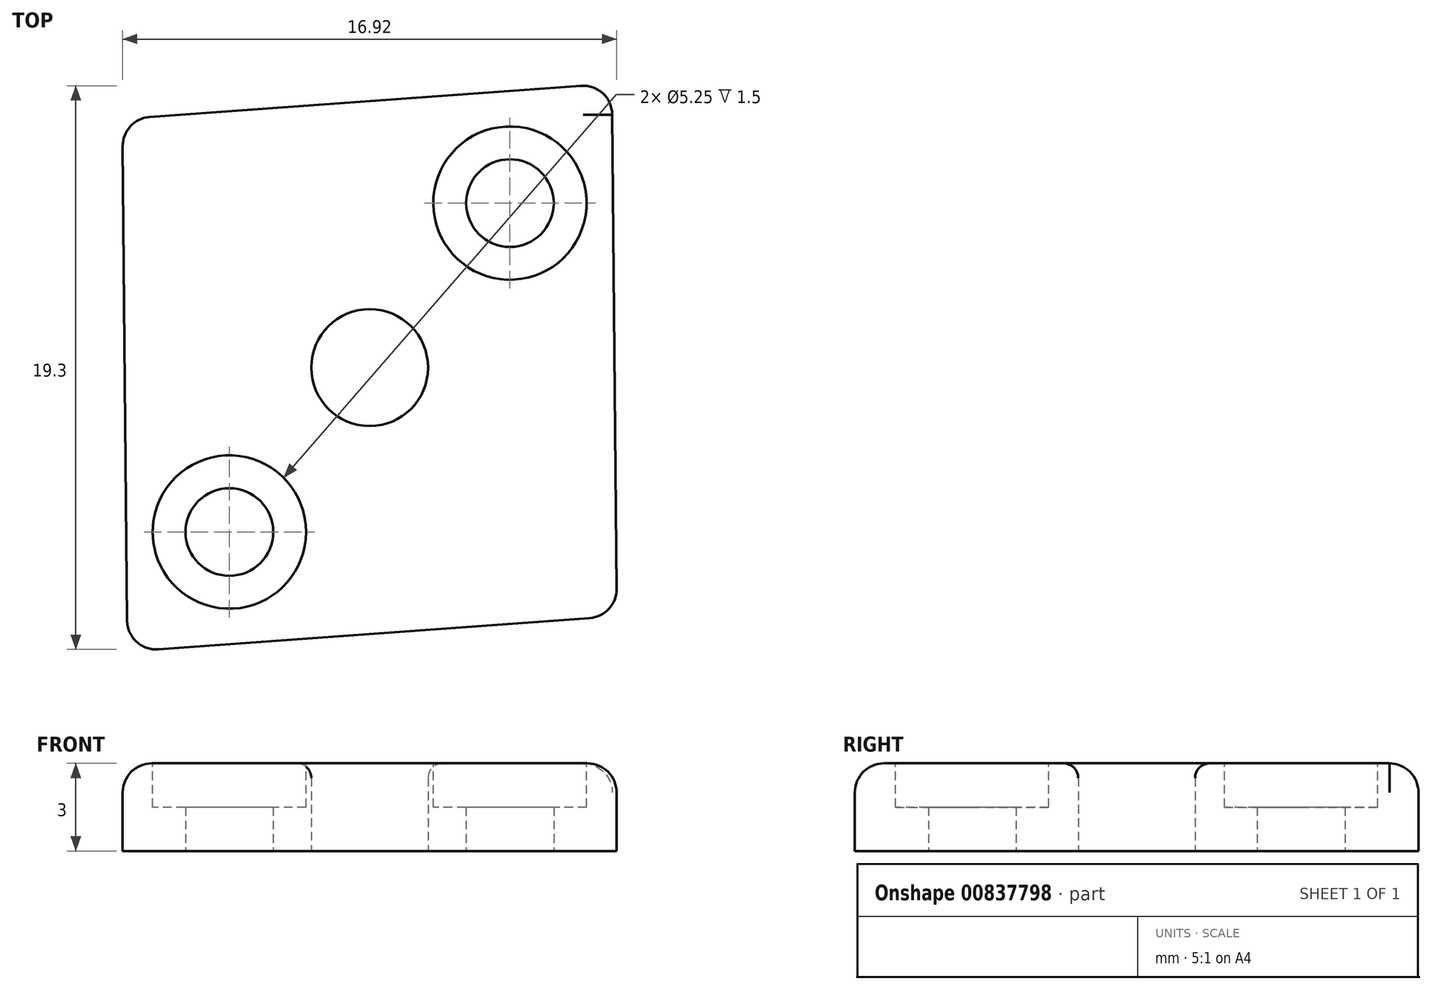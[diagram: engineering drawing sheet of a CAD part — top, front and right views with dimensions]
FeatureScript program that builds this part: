
annotation { "Feature Type Name" : "Feature", "Feature Type Description" : "" }
export const myFeature = defineFeature(function(context is Context, id is Id, definition is map)
    precondition{}
    {
        {
            var Q0;
            Q0=qCreatedBy(makeId("Top.planeOp"),FACE);
            var sketch = newSketch(context, id + "F0", { "sketchPlane" : qUnion([Q0])});
            skLineSegment(sketch, "E0", {"start": v(6.35, -6.39) * mm, "end": v(-6.35, 6.39) * mm, "construction": true});
            skLineSegment(sketch, "E1", {"start": v(6.35, 7.44) * mm, "end": v(-6.35, -7.44) * mm, "construction": true});
            skLineSegment(sketch, "E2", {"start": v(-6.35, -7.44) * mm, "end": v(-8.3, -9.73) * mm, "construction": true});
            skLineSegment(sketch, "E3", {"start": v(6.35, -6.39) * mm, "end": v(8.46, -8.51) * mm, "construction": true});
            skLineSegment(sketch, "E4", {"start": v(6.35, 7.44) * mm, "end": v(8.3, 9.73) * mm, "construction": true});
            skLineSegment(sketch, "E5", {"start": v(-6.35, 6.39) * mm, "end": v(-8.46, 8.51) * mm, "construction": true});
            skLineSegment(sketch, "E6", {"start": v(8.3, 9.73) * mm, "end": v(8.46, -8.51) * mm});
            skLineSegment(sketch, "E7", {"start": v(8.46, -8.51) * mm, "end": v(-8.3, -9.73) * mm});
            skLineSegment(sketch, "E8", {"start": v(-8.3, -9.73) * mm, "end": v(-8.46, 8.51) * mm});
            skLineSegment(sketch, "E9", {"start": v(-8.46, 8.51) * mm, "end": v(8.3, 9.73) * mm});
            skCircle(sketch, "E10", {"center": v(0, 0) * mm, "radius": 2 * mm});
            skLineSegment(sketch, "E11", {"start": v(0, 0) * mm, "end": v(-0.85, -1.8) * mm, "construction": true});
            skLineSegment(sketch, "E12", {"start": v(0, 0) * mm, "end": v(1.14, -1.64) * mm, "construction": true});
            skLineSegment(sketch, "E13", {"start": v(0, 0) * mm, "end": v(-1.14, 1.64) * mm, "construction": true});
            skLineSegment(sketch, "E14", {"start": v(0, 0) * mm, "end": v(0.85, 1.8) * mm, "construction": true});
            skLineSegment(sketch, "E15", {"start": v(-0.85, -1.8) * mm, "end": v(-1.72, -3.66) * mm, "construction": true});
            skLineSegment(sketch, "E16", {"start": v(0.85, 1.8) * mm, "end": v(1.72, 3.66) * mm, "construction": true});
            skLineSegment(sketch, "E17", {"start": v(-1.14, 1.64) * mm, "end": v(-2.3, 3.32) * mm, "construction": true});
            skLineSegment(sketch, "E18", {"start": v(1.14, -1.64) * mm, "end": v(2.3, -3.32) * mm, "construction": true});
            skLineSegment(sketch, "E19", {"start": v(6.35, 0.53) * mm, "end": v(-6.35, -0.53) * mm, "construction": true});
            skLineSegment(sketch, "E20", {"start": v(2.3, -3.32) * mm, "end": v(-1.72, -3.66) * mm});
            skLineSegment(sketch, "E21", {"start": v(1.72, 3.66) * mm, "end": v(-2.3, 3.32) * mm});
            skLineSegment(sketch, "E22", {"start": v(2, 0.17) * mm, "end": v(4.03, 0.34) * mm, "construction": true});
            skLineSegment(sketch, "E23", {"start": v(-2, -0.17) * mm, "end": v(-4.03, -0.34) * mm, "construction": true});
            skLineSegment(sketch, "E24", {"start": v(4.03, 0.34) * mm, "end": v(2.3, -3.32) * mm});
            skLineSegment(sketch, "E25", {"start": v(-1.72, -3.66) * mm, "end": v(-4.03, -0.34) * mm});
            skLineSegment(sketch, "E26", {"start": v(-4.03, -0.34) * mm, "end": v(-2.3, 3.32) * mm});
            skLineSegment(sketch, "E27", {"start": v(1.72, 3.66) * mm, "end": v(4.03, 0.34) * mm});
            skLineSegment(sketch, "E28", {"start": v(8.3, 9.73) * mm, "end": v(2.35, 2.75) * mm, "construction": true});
            skLineSegment(sketch, "E29", {"start": v(-2.35, -2.75) * mm, "end": v(-8.3, -9.73) * mm, "construction": true});
            skLineSegment(sketch, "E30", {"start": v(5.32, 6.24) * mm, "end": v(4.8, 5.63) * mm, "construction": true});
            skLineSegment(sketch, "E31", {"start": v(-5.32, -6.24) * mm, "end": v(-4.8, -5.63) * mm, "construction": true});
            skCircle(sketch, "E32", {"center": v(4.8, 5.63) * mm, "radius": 1.5 * mm});
            skCircle(sketch, "E33", {"center": v(-4.8, -5.63) * mm, "radius": 1.5 * mm});
            skSolve(sketch);
        }
        {
            var Q0;
            Q0 = qSketchRegion(id + "F0", true);
            var Q1;
            Q1=makeQuery(id+"F0.imprint","IMPRINT",FACE,{"disambiguationData":[TD([[makeQuery(id+"F0.imprint","IMPRINT",EDGE,{"derivedFrom":sQuery(id+"F0.wireOp",EDGE,"E10")}),-1.0]])]});
            extrude(context, id + "F1", {"entities" : qUnion([Q0, Q1]), "depth" : 3 * mm, "offsetDistance" : 25 * mm});
        }
        {
            var Q0;
            Q0=makeQuery(id+"F1.opExtrude","CAP_FACE",FACE,{"disambiguationData":[OSD([sQuery(id+"F0.wireOp",EDGE,"E6"),sQuery(id+"F0.wireOp",EDGE,"E7"),sQuery(id+"F0.wireOp",EDGE,"E8"),sQuery(id+"F0.wireOp",EDGE,"E9"),sQuery(id+"F0.wireOp",EDGE,"E10"),sQuery(id+"F0.wireOp",EDGE,"E32"),sQuery(id+"F0.wireOp",EDGE,"E33")])],"isStart":false});
            var sketch = newSketch(context, id + "F2", { "sketchPlane" : qUnion([Q0])});
            skCircle(sketch, "E34", {"center": v(-4.8, -5.63) * mm, "radius": 2.62 * mm});
            skCircle(sketch, "E35", {"center": v(4.8, 5.63) * mm, "radius": 2.62 * mm});
            skSolve(sketch);
        }
        {
            var Q0;
            Q0=makeQuery(id+"F2.imprint","IMPRINT",FACE,{"disambiguationData":[TD([[makeQuery(id+"F2.imprint","IMPRINT",EDGE,{"derivedFrom":sQuery(id+"F2.wireOp",EDGE,"E34")}),1.0]])]});
            var Q1;
            Q1=makeQuery(id+"F2.imprint","IMPRINT",FACE,{"disambiguationData":[TD([[makeQuery(id+"F2.imprint","IMPRINT",EDGE,{"derivedFrom":sQuery(id+"F2.wireOp",EDGE,"E35")}),1.0]])]});
            extrude(context, id + "F3", {"entities" : qUnion([Q0, Q1]), "operationType" : NewBodyOperationType.REMOVE, "oppositeDirection" : true, "depth" : 1.5 * mm, "offsetDistance" : 25 * mm});
        }
        {
            var Q0;
            Q0=makeQuery(id+"F1.opExtrude","SWEPT_EDGE",EDGE,{"disambiguationData":[OSD([sQuery(id+"F0.wireOp",EDGE,"E8"),sQuery(id+"F0.wireOp",EDGE,"E9")])]});
            var Q1;
            Q1=makeQuery(id+"F1.opExtrude","CAP_EDGE",EDGE,{"disambiguationData":[OSD([sQuery(id+"F0.wireOp",EDGE,"E8")])],"isStart":false});
            var Q2;
            Q2=makeQuery(id+"F1.opExtrude","CAP_EDGE",EDGE,{"disambiguationData":[OSD([sQuery(id+"F0.wireOp",EDGE,"E9")])],"isStart":false});
            var Q3;
            Q3=makeQuery(id+"F1.opExtrude","SWEPT_EDGE",EDGE,{"disambiguationData":[OSD([sQuery(id+"F0.wireOp",EDGE,"E6"),sQuery(id+"F0.wireOp",EDGE,"E9")])]});
            var Q4;
            Q4=makeQuery(id+"F1.opExtrude","CAP_EDGE",EDGE,{"disambiguationData":[OSD([sQuery(id+"F0.wireOp",EDGE,"E6")])],"isStart":false});
            var Q5;
            Q5=makeQuery(id+"F1.opExtrude","SWEPT_EDGE",EDGE,{"disambiguationData":[OSD([sQuery(id+"F0.wireOp",EDGE,"E6"),sQuery(id+"F0.wireOp",EDGE,"E7")])]});
            var Q6;
            Q6=makeQuery(id+"F1.opExtrude","CAP_EDGE",EDGE,{"disambiguationData":[OSD([sQuery(id+"F0.wireOp",EDGE,"E7")])],"isStart":false});
            var Q7;
            Q7=makeQuery(id+"F1.opExtrude","SWEPT_EDGE",EDGE,{"disambiguationData":[OSD([sQuery(id+"F0.wireOp",EDGE,"E7"),sQuery(id+"F0.wireOp",EDGE,"E8")])]});
            fillet(context, id + "F4", {"entities" : qUnion([Q0, Q1, Q2, Q3, Q4, Q5, Q6, Q7]), "radius" : 1 * mm, "tangentPropagation" : true, "allowEdgeOverflow" : false});
        }
        {
            var Q0;
            Q0=makeQuery(id+"F1.opExtrude","CAP_EDGE",EDGE,{"disambiguationData":[OSD([sQuery(id+"F0.wireOp",EDGE,"E10")])],"isStart":false});
            fillet(context, id + "F5", {"entities" : qUnion([Q0]), "radius" : .5 * mm, "tangentPropagation" : true, "allowEdgeOverflow" : false});
        }
    });
